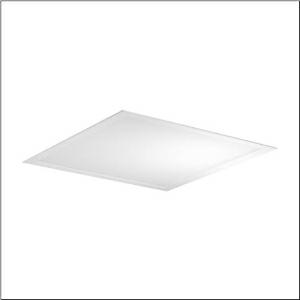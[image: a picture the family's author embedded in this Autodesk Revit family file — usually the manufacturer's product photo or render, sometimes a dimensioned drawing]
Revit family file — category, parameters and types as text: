
# Revit family: apollon_21_square_51mq11wd2t14
name_source: partatom
category: Lighting Fixtures
units: mm (PartAtom-declared; Revit-internal decimal feet)

## family parameters
Cut with Voids When Loaded = No
Host = Face
Light Source = No
Part Type = Normal
Room Calculation Point = No
Round Connector Dimension = Use Diameter
Shared = No

## types (1)
- --- (1 x LED 2700 K ... 6500 K, 4600 lm, 30.4 W, 4000K)
    Apparent Load = 30 VA
    CIE Flux Codes = 66 89 97 100 100
    Color Rendering = 80
    Color Temperature = 4000K
    Default Elevation = 1800 mm
    Description = Apollon 21 square, office luminaire, primary optical cover: micro prismatic cover, of PMMA, CAT 2 (L<= 3000cd/m²), light emission: direct distribution, primary light characteristic: symmetric, installation type: lay-in mounting, LED, rated luminous flux: 4.600lm, luminous efficacy: 151lm/W, light colour: 8tw, colour temperature: 2700..6500K, control gear: DALI-2 DT8, with terminal, 5-pole, mains connection: 220..240V, AC/DC, 0/50..60Hz, rated input power: 30.4W, housing, of aluminium, coated, traffic white (RAL 9016), module: M625, length: 620mm, width: 620mm, height: 55mm, recess depth: 180mm, housing upper side, of sheet steel, galvanised, protection rating (complete): IP20, protection rating (lamp compartment, on room side): IP50, insulation class (complete): insulation class II (safety insulation), certification: CE, ENEC, impact resistance: IK03, permissible operating ambient temperature: -20..+45°C, permissible storage temperature: -40..+80°C, standard: EN 60598-2-22, packaging unit: 1 piece
    Height = 0 mm  [stored 0 ft]
    Lamp = 1 x LED 2700 K ... 6500 K
    Lamp Light Flux = 4600 lm
    Lamp Power = 30.4 W
    Lamp count = 1
    Length = 620 mm
    Luminous efficacy = 151 lm/W
    Manufacturer = Siteco
    ModVariant = No
    Model = 51MQ11WD2T14
    Mounting Place = Ceiling
    Mounting Type = Recessed
    Number of Poles = 1
    OnlyDefault = Yes
    Power Factor = 1
    Product Name = Apollon 21 square
    Product group = office luminaire | ceiling recessed
    ProductGroupID = 401
    Protection Class = Protection class II
    Protection Degree = IP 20
    RLX_Detail_Level = 1
    RLX_Emergency_Light_Flux = 0 lm
    RLX_Emergency_Type = 0
    RLX_Emergency_Type_DB = No
    RlxData = <blob elided: 13053 chars, md5=cffdb86b>
    Socket = socket
    Standby Power = 0 W
    System Light Flux = 4600 lm
    System Power = 30 W
    Type Comments = factory setting: CCT=4000K, colour temperature 4000K
    Type Image = l_1291054.jpg
    URL = http://relux.com
    VarID = @adj_067500
    Voltage = 0 V
    Weight = 0.00 kg
    Width = 620 mm

note: [stored X ft] marks values corroborated as IEEE doubles in the binary element streams (Revit-internal decimal feet)

## geometry (parser evidence)
native form markers: Sweep x10
no freeform markers — native parametric forms only
